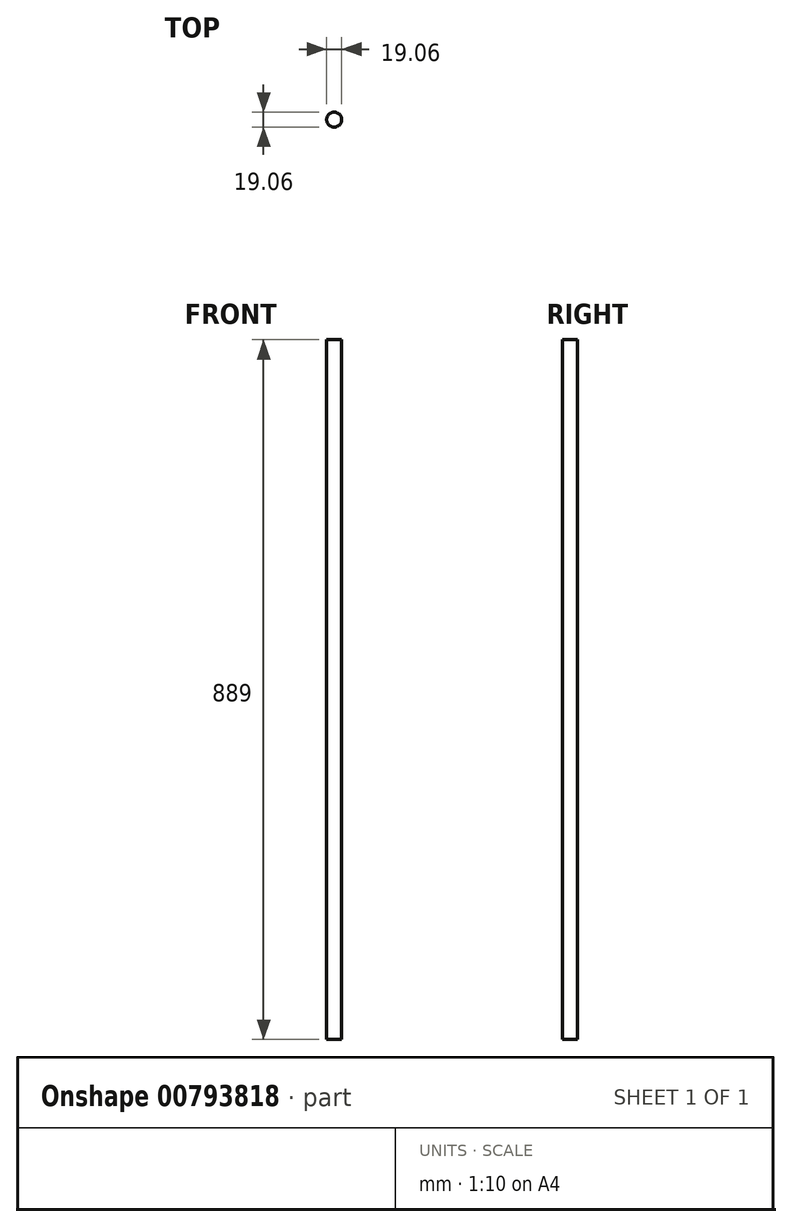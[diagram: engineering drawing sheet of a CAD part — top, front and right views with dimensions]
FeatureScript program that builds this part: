
annotation { "Feature Type Name" : "Feature", "Feature Type Description" : "" }
export const myFeature = defineFeature(function(context is Context, id is Id, definition is map)
    precondition{}
    {
        {
            var Q0;
            Q0=qCreatedBy(makeId("Top.planeOp"),FACE);
            var sketch = newSketch(context, id + "F0", { "sketchPlane" : qUnion([Q0])});
            skCircle(sketch, "E0", {"center": v(0, 0) * mm, "radius": 9.53 * mm});
            skSolve(sketch);
        }
        {
            var Q0;
            Q0 = qSketchRegion(id + "F0", true);
            extrude(context, id + "F1", {"entities" : qUnion([Q0]), "depth" : 889 * mm, "offsetDistance" : 25.4 * mm});
        }
    });
